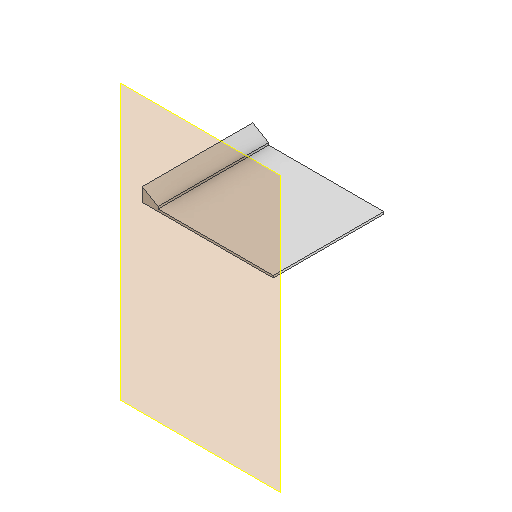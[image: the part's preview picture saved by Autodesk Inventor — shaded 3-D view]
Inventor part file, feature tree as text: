
AUTODESK INVENTOR PART (.ipt)
format: ipt  version: 2022 (Build 260153000, 153)  size: 101,888 bytes
history: native  units: mm
features: reference x5, plane x2, other x2, sketch x1, extrude x1
ambient origin geometry x8: Origin, YZ Plane, XZ Plane, XY Plane, X Axis, Y Axis, Z Axis, Center Point
bodies: Volumenkörper1 (feature_tree)
feature tree (11):
  plane  "Arbeitsebene1"
  sketch  "Skizze1"  dims[d0=0.2mm d1=10.0mm d2=0.0mm d3=0.5mm d4=1.404145mm]
  plane  "Arbeitsebene2"
  extrude  "Extrusion1"  Depth=0.5mm TaperAngle=0.0deg
  reference  "Referenz1"
  reference  "Referenz2"
  reference  "Referenz3"
  reference  "Referenz4"
  reference  "Referenz5"
  other  "Assembly_Matchboxscope_injectionmolded.iam"
  other  "IM_ledmatrix_holder:1"
